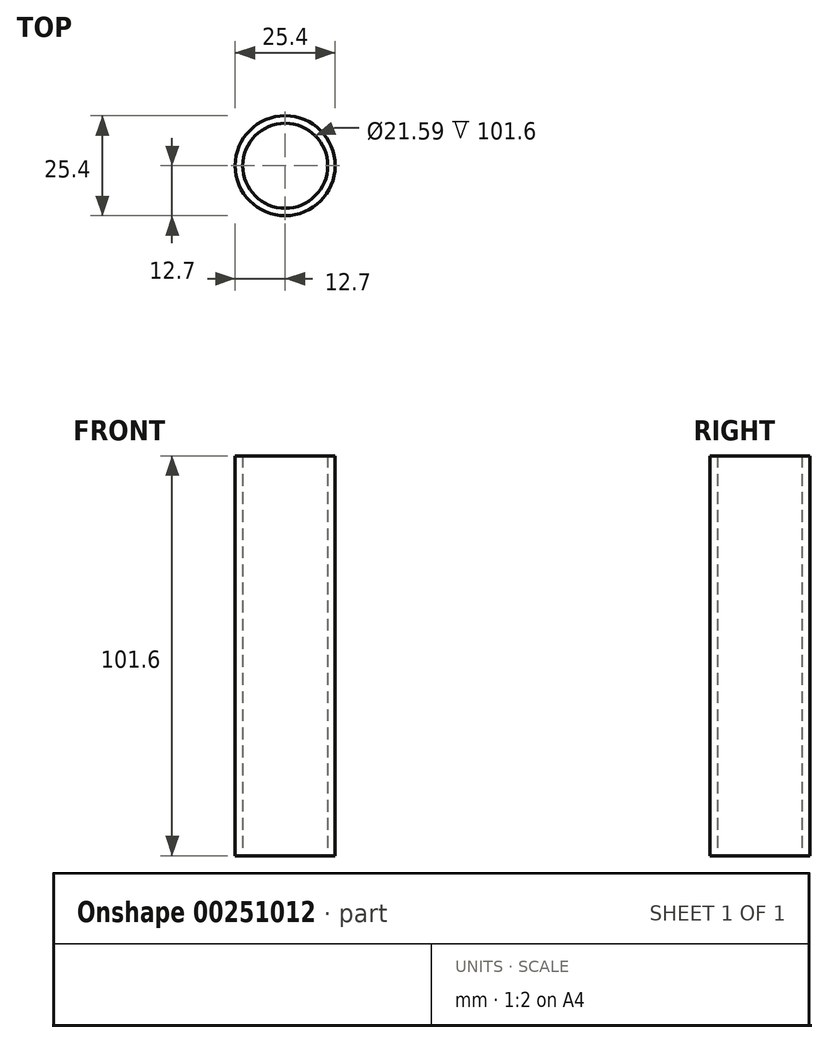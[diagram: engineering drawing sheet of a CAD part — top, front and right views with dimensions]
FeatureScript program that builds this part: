
annotation { "Feature Type Name" : "Feature", "Feature Type Description" : "" }
export const myFeature = defineFeature(function(context is Context, id is Id, definition is map)
    precondition{}
    {
        {
            var Q0;
            Q0=qCreatedBy(makeId("Top.planeOp"),FACE);
            var sketch = newSketch(context, id + "F0", { "sketchPlane" : qUnion([Q0])});
            skCircle(sketch, "E0", {"center": v(0, 0) * mm, "radius": 12.7 * mm});
            skCircle(sketch, "E1", {"center": v(0, 0) * mm, "radius": 10.8 * mm});
            skSolve(sketch);
        }
        {
            var Q0;
            Q0=makeQuery(id+"F0.imprint","IMPRINT",FACE,{"disambiguationData":[TD([[makeQuery(id+"F0.imprint","IMPRINT",EDGE,{"derivedFrom":sQuery(id+"F0.wireOp",EDGE,"E0")}),1.0]])]});
            extrude(context, id + "F1", {"entities" : qUnion([Q0]), "depth" : 101.6 * mm});
        }
    });
